# Revit family: LLF
name_source: partatom
category: Lighting Fixtures
revit_build: Autodesk Revit 2014 (Build: 20130308_1515(x64)
units: mm (PartAtom-declared; Revit-internal decimal feet)

## types (1)
- LLF
    Apparent Load = 21 VA
    Assembly Code = D5020200
    Color Filter = 16777215
    Default Elevation = 48 "
    Description = Low Level Flood
    Dimming Lamp Color Temperature Shift = <None>
    Emit Shape Visible in Rendering = No
    Emit from Rectangle Length = 6 "
    Emit from Rectangle Width = 10 "
    Glass = Hubbell - Glass
    Is 120V = Yes
    Is 270V = No
    Keynote = Lighting
    Lamp = LED
    Load Classification = Lighting
    Manufacturer = Kim Lighting
    Model = LLF
    Photometric Web File = llf10p35-20l3k.ies
    Product Documentation Link = https://hubbellcdn.com
    Product Link = https://www.hubbell.com
    Product Material = Paint - Hubbell - Basic Black
    Tilt Angle = 90.00°
    Type Comments = Flood Light
    URL = https://www.hubbell.com
    Voltage = 120 V
    Watt = 21 W
    Wattage Comments = 21W

## geometry (parser evidence)
native form markers: Sweep x1
no freeform markers — native parametric forms only
